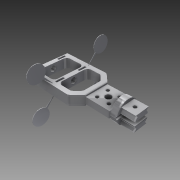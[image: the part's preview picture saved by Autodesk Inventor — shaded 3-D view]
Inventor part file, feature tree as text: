
AUTODESK INVENTOR PART (.ipt)
format: ipt  version: 2014 (Build 180170000, 170)  size: 421,888 bytes
history: native  units: mm
features: extrude x9, sketch x7, fillet x4, mirror x3, projected_geometry x3, plane x2, pattern_linear x1
ambient origin geometry x8: Origin, YZ Plane, XZ Plane, XY Plane, X Axis, Y Axis, Z Axis, Center Point
bodies: Solid1 (feature_tree)
feature tree (29):
  plane  "Work Plane1"
  extrude  "Extrusion7"  Depth=4.4mm
  extrude  "Extrusion8"  Depth=7.2mm
  extrude  "Extrusion9"  Depth=28.0mm
  fillet  "Fillet1"  Radius=22.5mm
  fillet  "Fillet4"  Radius=7.35mm
  extrude  "Extrusion10"  Depth=4.0mm
  extrude  "Extrusion13"  Depth=4.0mm
  mirror  "Mirror4"
  fillet  "Fillet8"  Radius=4.0mm
  fillet  "Fillet9"  Radius=14.0mm
  extrude  "Extrusion15"  Depth=13.9192mm
  extrude  "Extrusion16"  Depth=10.0mm
  pattern_linear  "Rectangular Pattern1"  Spacing1=6.0mm  [1 undecoded]
  plane  "Work Plane3"
  extrude  "Extrusion17"  TaperAngle=135.0deg  [1 undecoded]
  mirror  "Mirror1"
  mirror  "Mirror2"
  extrude  "Extrusion11"  TaperAngle=135.0deg  [1 undecoded]
  sketch  "Sketch8"  dims[d0=5.0mm d6=4.4mm d12=4.4mm d14=4.4mm]
  sketch  "Sketch9"  dims[d49=7.2mm d50=28.0mm]
  projected_geometry  "Projected Loop1"
  projected_geometry  "Projected Loop2"
  sketch  "Sketch10"  dims[d51=14.0mm d52=28.0mm d53=22.5mm d54=7.35mm]
  sketch  "Sketch12"  dims[d55=14.0mm d56=14.0mm d59=14.0mm d63=4.0mm]
  sketch  "Sketch14"  dims[d64=4.0mm d65=4.0mm d66=4.0mm d71=14.0mm]
  sketch  "Sketch15"  dims[d72=14.0mm d73=13.9192mm]
  sketch  "Sketch16"  dims[d74=8.0mm d75=0.0mm d77=6.0mm d78=6.0mm d79=135.0deg d80=135.0deg d84=38.0mm d85=6.0mm d86=6.0mm d91=25.0mm d92=25.0mm d93=6.0mm d94=6.0mm d96=12.35mm d97=0.0mm d98=7.35mm d99=25.0mm d100=25.0mm d101=6.175mm d102=6.175mm d103=5.0mm d105=65.0mm d106=0.0mm d108=1.0mm d109=4.0mm d110=4.0mm d111=26.0mm d113=2.0mm d114=2.0mm d115=45.0deg d116=45.0deg d117=22.5mm d118=0.0mm d121=18.384776mm d122=50.0mm d123=0.0mm d127=15.0mm d128=0.0mm d139=1.0mm d140=4.0mm d141=1.0mm d149=13.9192mm d150=6.9596mm d151=6.9596mm d152=6.9596mm d153=6.9596mm d154=7.5mm d155=4.0mm d156=20.0mm d157=0.0mm d159=5.6875mm d160=5.6625mm d161=5.6625mm d163=10.0mm d167=2.5mm d168=15.0mm d169=0.0mm d170=20.0mm d172=31.0mm d173=5.6625mm d174=5.6625mm d175=10.0mm d176=1.75mm d177=1.75mm d178=-84.5mm d179=15.0mm d180=15.0mm d181=10.0mm d182=1.570796mm d183=7.068583mm d184=22.5mm d185=0.6mm d186=0.0mm d187=4.0mm d188=0.2mm d189=0.2mm d190=0.4mm d191=0.4mm d192=0.4mm d193=0.4mm d194=0.2mm d195=0.4mm d196=0.4mm d199=11.0mm d200=11.0mm d202=6.0mm d203=1.0mm]
  projected_geometry  "Projected Loop3"
note: 3 required parameter values undecoded (feature->parameter linkage not recoverable at this tier; creation-order binding heuristic only, values carry confidence <= 0.55)
